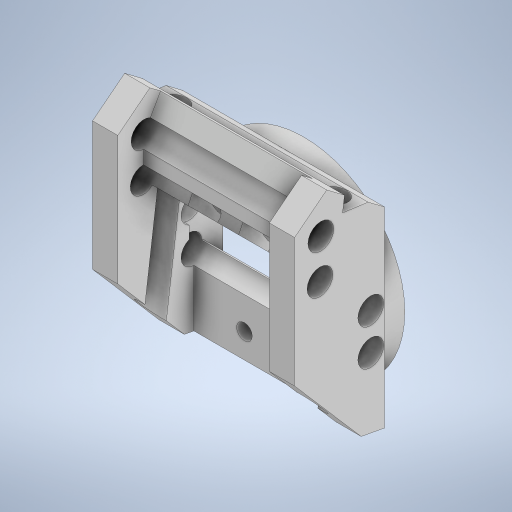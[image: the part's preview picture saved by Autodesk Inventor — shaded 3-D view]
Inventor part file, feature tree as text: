
AUTODESK INVENTOR PART (.ipt)
format: ipt  version: 2023.4 (Build 274418000, 418)  size: 417,280 bytes
history: native  units: mm
features: extrude x8, sketch x8, chamfer x2, plane x1
ambient origin geometry x8: Origin, YZ Plane, XZ Plane, XY Plane, X Axis, Y Axis, Z Axis, Center Point
bodies: Solid1 (feature_tree)
feature tree (19):
  extrude  "Extrusion1"  Depth=4.0mm TaperAngle=0.0deg
  extrude  "Extrusion2"  Depth=5.1mm
  extrude  "Extrusion3"  Depth=5.1mm
  extrude  "Extrusion4"  Depth=3.6mm
  extrude  "Extrusion5"  Depth=30.0mm TaperAngle=0.0deg
  chamfer  "Chamfer1"  [1 undecoded]
  extrude  "Extrusion6"  Depth=2.9mm TaperAngle=0.0deg
  plane  "Work Plane1"
  extrude  "Extrusion7"  Depth=2.9mm TaperAngle=45.0deg
  extrude  "Extrusion8"  TaperAngle=0.0deg  [1 undecoded]
  chamfer  "Chamfer2"  [1 undecoded]
  sketch  "Sketch1"  dims[d0=40.0mm d1=4.0mm d2=0.0mm]
  sketch  "Sketch2"  dims[d3=5.1mm d4=5.1mm]
  sketch  "Sketch3"  dims[d5=5.1mm d7=5.1mm]
  sketch  "Sketch4"  dims[d8=3.6mm d9=3.6mm]
  sketch  "Sketch5"  dims[d10=40.0mm d11=0.0mm d12=30.0mm d13=0.0mm]
  sketch  "Sketch6"  dims[d14=5.1mm]
  sketch  "Sketch7"  dims[d15=5.1mm d16=0.0mm d17=0.0mm]
  sketch  "Sketch8"  dims[d18=15.8mm d19=32.0mm d20=0.0mm d21=3.9mm d22=2.0mm d23=45.0deg d24=0.0mm d25=0.0mm d26=-11.0mm d27=6.0mm d28=6.0mm d29=10.0mm d30=0.0mm d31=6.0mm d32=6.0mm d33=6.0mm d34=6.0mm d35=2.9mm d36=0.0mm d37=1.0mm d38=2.0mm d39=45.0deg]
note: 3 required parameter values undecoded (feature->parameter linkage not recoverable at this tier; creation-order binding heuristic only, values carry confidence <= 0.55)
